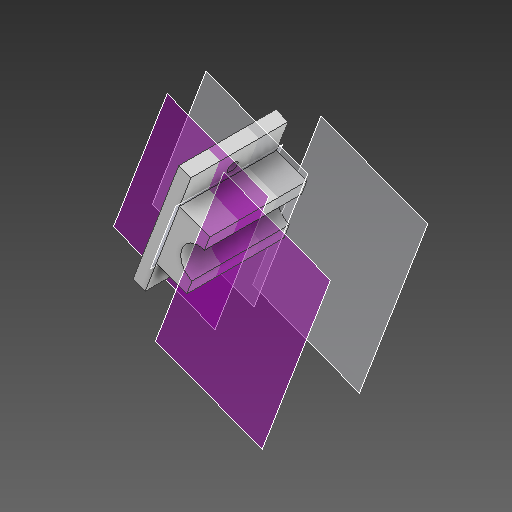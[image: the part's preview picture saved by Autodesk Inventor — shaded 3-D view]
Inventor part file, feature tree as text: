
AUTODESK INVENTOR PART (.ipt)
format: ipt  version: 2021 (Build 250183000, 183)  size: 152,064 bytes
history: native  units: in
note: dims shown in document units (in); Inventor stores cm internally (conversion verified against a paired STEP export)
features: other x5, sketch x5, plane x4
ambient origin geometry x8: Origin, YZ Plane, XZ Plane, XY Plane, X Axis, Y Axis, Z Axis, Center Point
bodies: Solid1 (feature_tree), Solid2 (feature_tree), Solid3 (feature_tree)
feature tree (14):
  other  "Soporte Superior Tubos.ipt"
  other  "Solid1::Soporte Superior Tubos.ipt"
  other  "Solid2::Soporte Superior Tubos.ipt"
  other  "Solid3::Soporte Superior Tubos.ipt"
  other  "TaggingFeature1"
  sketch  "Sketch1"  dims[d0=0.3937in]
  sketch  "Sketch2"
  sketch  "Sketch3"
  sketch  "Sketch4"
  sketch  "Sketch5"
  plane  "Work Plane1"
  plane  "Work Plane2"
  plane  "Work Plane3"
  plane  "Work Plane6"
